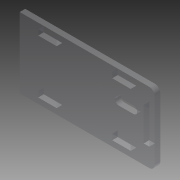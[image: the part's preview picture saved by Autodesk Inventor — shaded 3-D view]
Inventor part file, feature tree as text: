
AUTODESK INVENTOR PART (.ipt)
format: ipt  version: 2015 (Build 190159000, 159)  size: 168,960 bytes
history: native  units: mm
features: sketch x3, extrude x2, projected_geometry x2, fillet x1
ambient origin geometry x8: Origin, YZ Plane, XZ Plane, XY Plane, X Axis, Y Axis, Z Axis, Center Point
bodies: Solid1 (feature_tree)
feature tree (8):
  extrude  "Extrusion1"  Depth=38.0mm
  fillet  "Fillet1"  Radius=3.0mm
  extrude  "Extrusion2"  Depth=3.0mm
  sketch  "Sketch3"  dims[d6=10.0mm d7=10.0mm d8=18.0mm d9=32.0mm d10=3.0mm d11=3.0mm d12=3.0mm d13=10.0mm d14=13.0mm d15=3.0mm d16=0.0mm d17=3.0mm d21=2.0mm d22=8.0mm d23=11.5mm d24=3.0mm d25=0.0mm d26=15.0mm]
  sketch  "Sketch1"  dims[d0=73.0mm d1=38.0mm d3=3.0mm]
  sketch  "Sketch2"  dims[d4=3.0mm d5=3.0mm]
  projected_geometry  "Projected Loop1"
  projected_geometry  "Projected Loop2"
